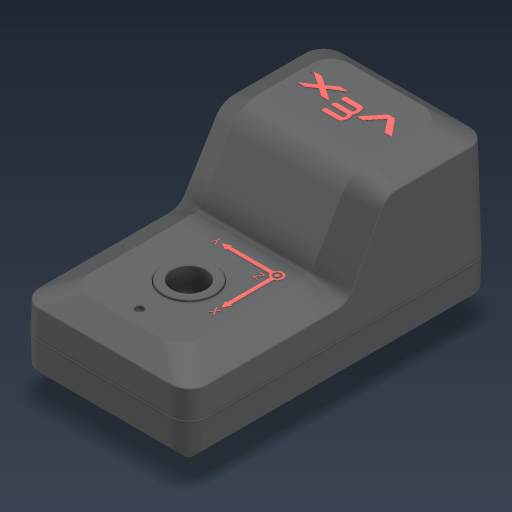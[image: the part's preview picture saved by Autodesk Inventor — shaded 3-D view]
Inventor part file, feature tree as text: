
AUTODESK INVENTOR PART (.ipt)
format: ipt  version: 2023 (Build 270158000, 158)  size: 1,014,272 bytes
history: native  units: in
note: dims shown in document units (in); Inventor stores cm internally (conversion verified against a paired STEP export)
features: other x3, extrude x2, sketch x2
ambient origin geometry x8: Origin, YZ Plane, XZ Plane, XY Plane, X Axis, Y Axis, Z Axis, Center Point
bodies: Solid1 (feature_tree), Solid2 (feature_tree), Solid3 (feature_tree)
feature tree (7):
  extrude  "Extrusion1"  TaperAngle=0.0deg  [1 undecoded]
  extrude  "Extrusion2"  Depth=0.0197in
  sketch  "Sketch2"  dims[d0=0.0in d1=0.0in]
  sketch  "Sketch3"  dims[d11=0.002in d12=0.0in d13=0.0197in d14=0.0787in d15=0.0787in d16=0.0591in d17=0.0394in d18=0.0098in d19=0.0394in d20=0.0197in d21=0.0197in d22=0.0197in d23=0.002in d24=0.0in]
  other  "276-4855-001 Rev2 - Web_1:1"
  other  "276-4855-002 Rev2 - Web_2:1"
  other  "276-4840-902 Rev1 - Web_3:1"
note: 1 required parameter value undecoded (feature->parameter linkage not recoverable at this tier; creation-order binding heuristic only, values carry confidence <= 0.55)
